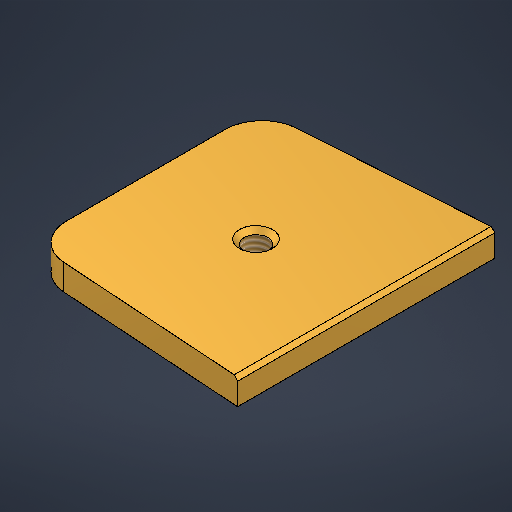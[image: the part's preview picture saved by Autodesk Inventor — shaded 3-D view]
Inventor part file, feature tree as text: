
AUTODESK INVENTOR PART (.ipt)
format: ipt  version: 2025.3 (Build 293356000, 356)  size: 208,384 bytes
history: native  units: mm
features: chamfer x2, sketch x1, extrude x1, hole x1, fillet x1
ambient origin geometry x8: Origin, YZ Plane, XZ Plane, XY Plane, X Axis, Y Axis, Z Axis, Center Point
bodies: Solid1 (feature_tree)
feature tree (6):
  sketch  "Sketch1"  dims[d1=30.0mm d2=35.0mm d3=4.0mm d4=0.0mm d5=3.242mm d6=8.0mm d7=4.5mm d8=6.8mm d9=90.0deg d10=8.0mm d11=20.594885mm d12=0.25mm d13=2.0mm d14=45.0deg d15=5.0mm d16=0.5mm d17=2.0mm d18=45.0deg d19=31.0mm d20=30.0mm]
  extrude  "Extrusion1"  Depth=30.0mm
  hole  "Hole1"  [1 undecoded]
  chamfer  "Chamfer1"  Distance=0.25mm Angle=45.0deg
  fillet  "Fillet1"  Radius=5.0mm
  chamfer  "Chamfer2"  Distance=0.5mm Angle=45.0deg
note: 1 required parameter value undecoded (feature->parameter linkage not recoverable at this tier; creation-order binding heuristic only, values carry confidence <= 0.55)
